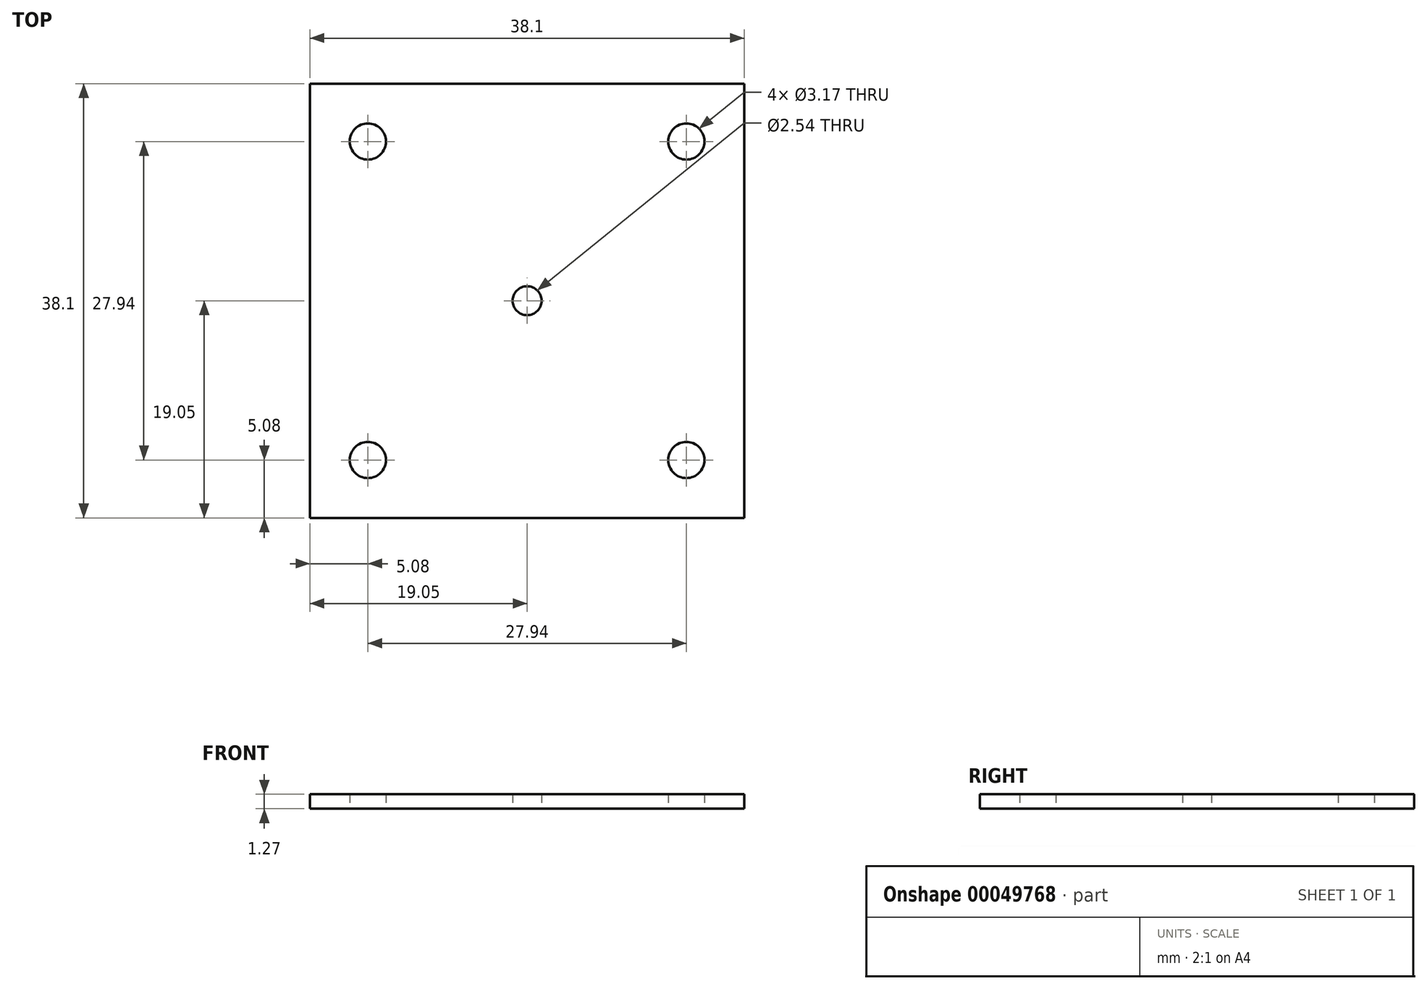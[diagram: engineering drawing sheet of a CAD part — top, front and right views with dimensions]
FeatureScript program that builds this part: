
annotation { "Feature Type Name" : "Feature", "Feature Type Description" : "" }
export const myFeature = defineFeature(function(context is Context, id is Id, definition is map)
    precondition{}
    {
        {
            var Q0;
            Q0=qCreatedBy(makeId("Top.planeOp"),FACE);
            var sketch = newSketch(context, id + "F0", { "sketchPlane" : qUnion([Q0])});
            skLineSegment(sketch, "E0.rect.bottom", {"start": v(19.05, -19.05) * mm, "end": v(-19.05, -19.05) * mm});
            skLineSegment(sketch, "E0.rect.top", {"start": v(19.05, 19.05) * mm, "end": v(-19.05, 19.05) * mm});
            skLineSegment(sketch, "E0.rect.left", {"start": v(19.05, -19.05) * mm, "end": v(19.05, 19.05) * mm});
            skLineSegment(sketch, "E0.rect.right", {"start": v(-19.05, -19.05) * mm, "end": v(-19.05, 19.05) * mm});
            skPoint(sketch, "E0.rect.middle", {"position": v(0, 0) * mm});
            skSolve(sketch);
        }
        {
            var Q0;
            Q0=qSketchRegion(id+"F0",true);
            extrude(context, id + "F1", {"entities" : qUnion([Q0]), "depth" : 1.27 * mm});
        }
        {
            var Q0;
            Q0=qCreatedBy(makeId("Top.planeOp"),FACE);
            var sketch = newSketch(context, id + "F2", { "sketchPlane" : qUnion([Q0])});
            skCircle(sketch, "E1", {"center": v(0, 0) * mm, "radius": 1.27 * mm});
            skSolve(sketch);
        }
        {
            var Q0;
            Q0=qSketchRegion(id+"F2",true);
            extrude(context, id + "F3", {"entities" : qUnion([Q0]), "operationType" : NewBodyOperationType.REMOVE, "depth" : 25.4 * mm});
        }
        {
            var Q0;
            Q0=qCreatedBy(makeId("Top.planeOp"),FACE);
            var sketch = newSketch(context, id + "F4", { "sketchPlane" : qUnion([Q0])});
            skCircle(sketch, "E2", {"center": v(13.97, 13.97) * mm, "radius": 1.59 * mm});
            skSolve(sketch);
        }
        {
            var Q0;
            Q0 = qSketchRegion(id + "F4", true);
            extrude(context, id + "F5", {"entities" : qUnion([Q0]), "operationType" : NewBodyOperationType.REMOVE, "depth" : 25.4 * mm});
        }
        {
            var Q0;
            Q0=makeQuery(id+"F1.opExtrude","SWEPT_BODY",BODY,{"disambiguationData":[OSD([sQuery(id+"F0.wireOp",EDGE,"E0.rect.bottom"),sQuery(id+"F0.wireOp",EDGE,"E0.rect.top"),sQuery(id+"F0.wireOp",EDGE,"E0.rect.left"),sQuery(id+"F0.wireOp",EDGE,"E0.rect.right")])]});
            var Q1;
            Q1=qCreatedBy(makeId("Right.planeOp"),FACE);
            mirror(context, id + "F6", {"operationType" : NewBodyOperationType.INTERSECT, "entities" : qUnion([Q0]), "mirrorPlane" : qUnion([Q1])});
        }
        {
            var Q0;
            Q0=makeQuery(id+"F1.opExtrude","SWEPT_BODY",BODY,{"disambiguationData":[OSD([sQuery(id+"F0.wireOp",EDGE,"E0.rect.bottom"),sQuery(id+"F0.wireOp",EDGE,"E0.rect.top"),sQuery(id+"F0.wireOp",EDGE,"E0.rect.left"),sQuery(id+"F0.wireOp",EDGE,"E0.rect.right")])]});
            var Q1;
            Q1=qCreatedBy(makeId("Front.planeOp"),FACE);
            mirror(context, id + "F7", {"operationType" : NewBodyOperationType.INTERSECT, "entities" : qUnion([Q0]), "mirrorPlane" : qUnion([Q1])});
        }
    });
